# Revit family: Light_Fixture-Ceiling_Mount-KOHLER-Purist-K-27267_1
name_source: partatom
category: Lighting Fixtures
revit_build: Autodesk Revit 2017 (Build: 20160225_1515(x64)
units: mm (PartAtom-declared; Revit-internal decimal feet)

## family parameters
Cut with Voids When Loaded = No
Host = Face
Light Source = Yes
OmniClass Number = 23.35.47.11
OmniClass Title = Lighting Fixtures
Part Type = Normal
Room Calculation Point = No
Round Connector Dimension = Use Diameter
Shared = No

## types (2) — shared parameters
ADA Compliant = No
Apparent Load = 0 VA
Assembly Code = D5040.50
Color Filter = 16777215
Date Modified = 07/01/2021
Default Elevation = 0"
Description = LINEAR LED CHANDELIER
Dimming Lamp Color Temperature Shift = Incandescent Lamp Curve
Electrical Connector = Yes
Electrical Note = One Dedicated Circuiy Required
Emit from Line Length = 30"
Hardware Included = No
Lamp = LED
Length = 5"
Light Source Symbol Size = 9"
Manufacturer = KOHLER Co.
Master Format 2014 = 26 51 13
Master Format 2014 Name = Interior Lighting Fixtures, Lamps, And Ballasts
Material = Premium Metal Construction
Product Documentation Link = https://www.us.kohler.com
Product Name = Purist
Product Page URL = http://www.us.kohler.com
URL = https://www.us.kohler.com
Voltage = 120 V
WaterSense Certified = No
Width = 33 15/16"

## per-type parameters (varying)
| type | Finish | Model | Type |
| 2GL-Brushed Moderne Brass | KOHLER-Metal-2GL-Brushed_Modern_Brass | K-27267-CHLED-2GL | 1 |
| BLL-Matte Black | KOHLER-Metal-BLL-Matte_Black | K-27267-CHLED-BLL | 2 |

## geometry (parser evidence)
native form markers: Sweep x5
no freeform markers — native parametric forms only
